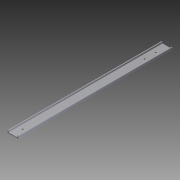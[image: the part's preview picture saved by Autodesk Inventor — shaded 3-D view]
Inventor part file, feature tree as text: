
AUTODESK INVENTOR PART (.ipt)
format: ipt  version: 2011 (Build 150239000, 239)  size: 91,648 bytes
history: native  units: in
note: dims shown in document units (in); Inventor stores cm internally (conversion verified against a paired STEP export)
features: extrude x2, sketch x2
ambient origin geometry x8: Origin, YZ Plane, XZ Plane, XY Plane, X Axis, Y Axis, Z Axis, Center Point
bodies: Solid1 (feature_tree)
feature tree (4):
  extrude  "Extrusion1"  Depth=0.374in
  extrude  "Extrusion2"  Depth=17.5197in TaperAngle=0.0deg
  sketch  "Sketch1"  dims[d0=1.3898in d1=0.374in]
  sketch  "Sketch2"  dims[d2=135.0deg d3=17.5197in d4=0.0in d5=1.1142in d6=0.1693in d7=13.8583in d8=15.1181in d9=17.5197in d10=0.0in]
